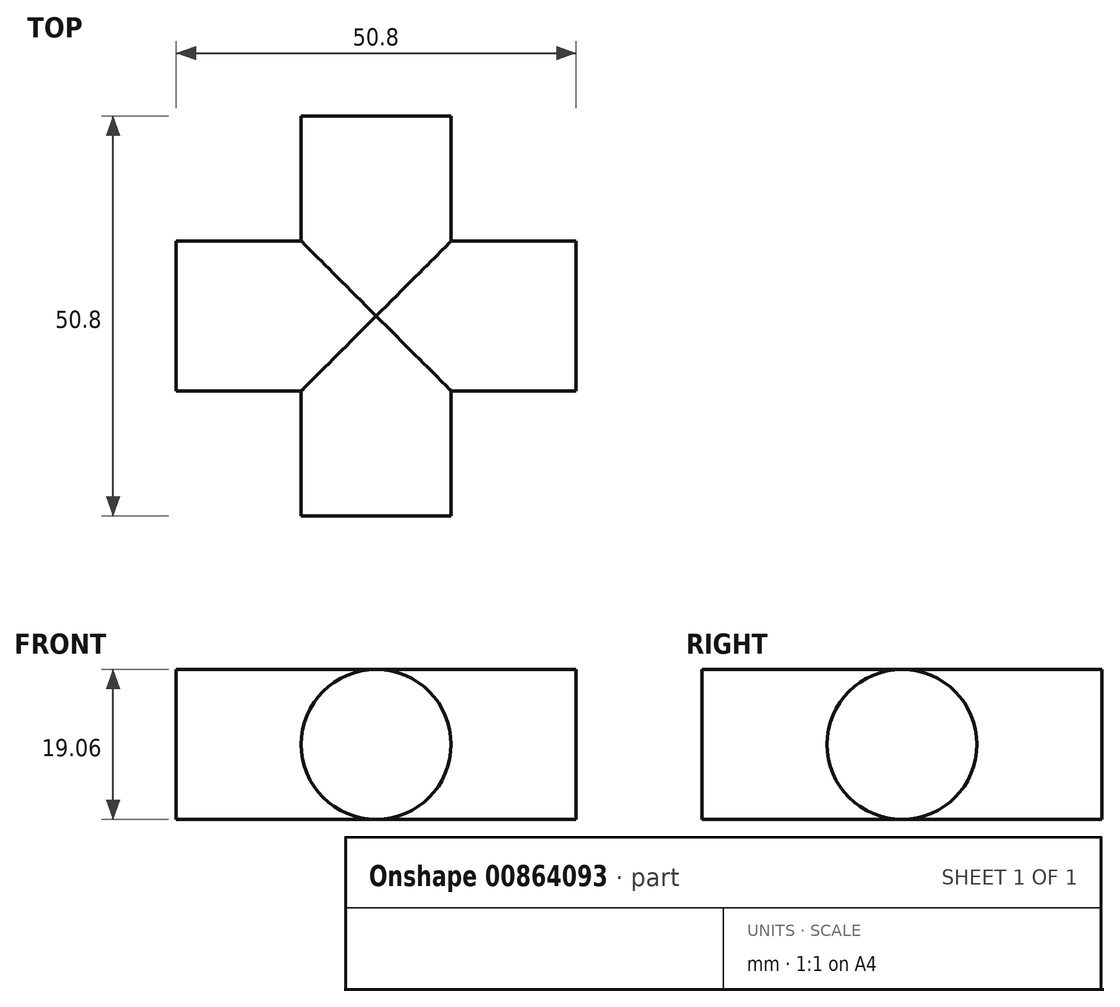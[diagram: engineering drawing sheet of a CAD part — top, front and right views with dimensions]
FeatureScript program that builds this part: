
annotation { "Feature Type Name" : "Feature", "Feature Type Description" : "" }
export const myFeature = defineFeature(function(context is Context, id is Id, definition is map)
    precondition{}
    {
        {
            var Q0;
            Q0=qCreatedBy(makeId("Front.planeOp"),FACE);
            var sketch = newSketch(context, id + "F0", { "sketchPlane" : qUnion([Q0])});
            skCircle(sketch, "E0", {"center": v(0, 0) * mm, "radius": 9.53 * mm});
            skSolve(sketch);
        }
        {
            var Q0;
            Q0=qCreatedBy(makeId("Right.planeOp"),FACE);
            var sketch = newSketch(context, id + "F1", { "sketchPlane" : qUnion([Q0])});
            skCircle(sketch, "E1", {"center": v(0, 0) * mm, "radius": 9.53 * mm});
            skSolve(sketch);
        }
        {
            var Q0;
            Q0=makeQuery(id+"F1.imprint","IMPRINT",FACE,{"disambiguationData":[TD([[makeQuery(id+"F1.imprint","IMPRINT",EDGE,{"derivedFrom":sQuery(id+"F1.wireOp",EDGE,"E1")}),1.0]])]});
            extrude(context, id + "F2", {"entities" : qUnion([Q0]), "depth" : 50.8 * mm, "offsetDistance" : 25.4 * mm, "symmetric" : true});
        }
        {
            var Q0;
            Q0 = qSketchRegion(id + "F0", true);
            extrude(context, id + "F3", {"entities" : qUnion([Q0]), "operationType" : NewBodyOperationType.ADD, "depth" : 50.8 * mm, "offsetDistance" : 25.4 * mm, "symmetric" : true});
        }
    });
